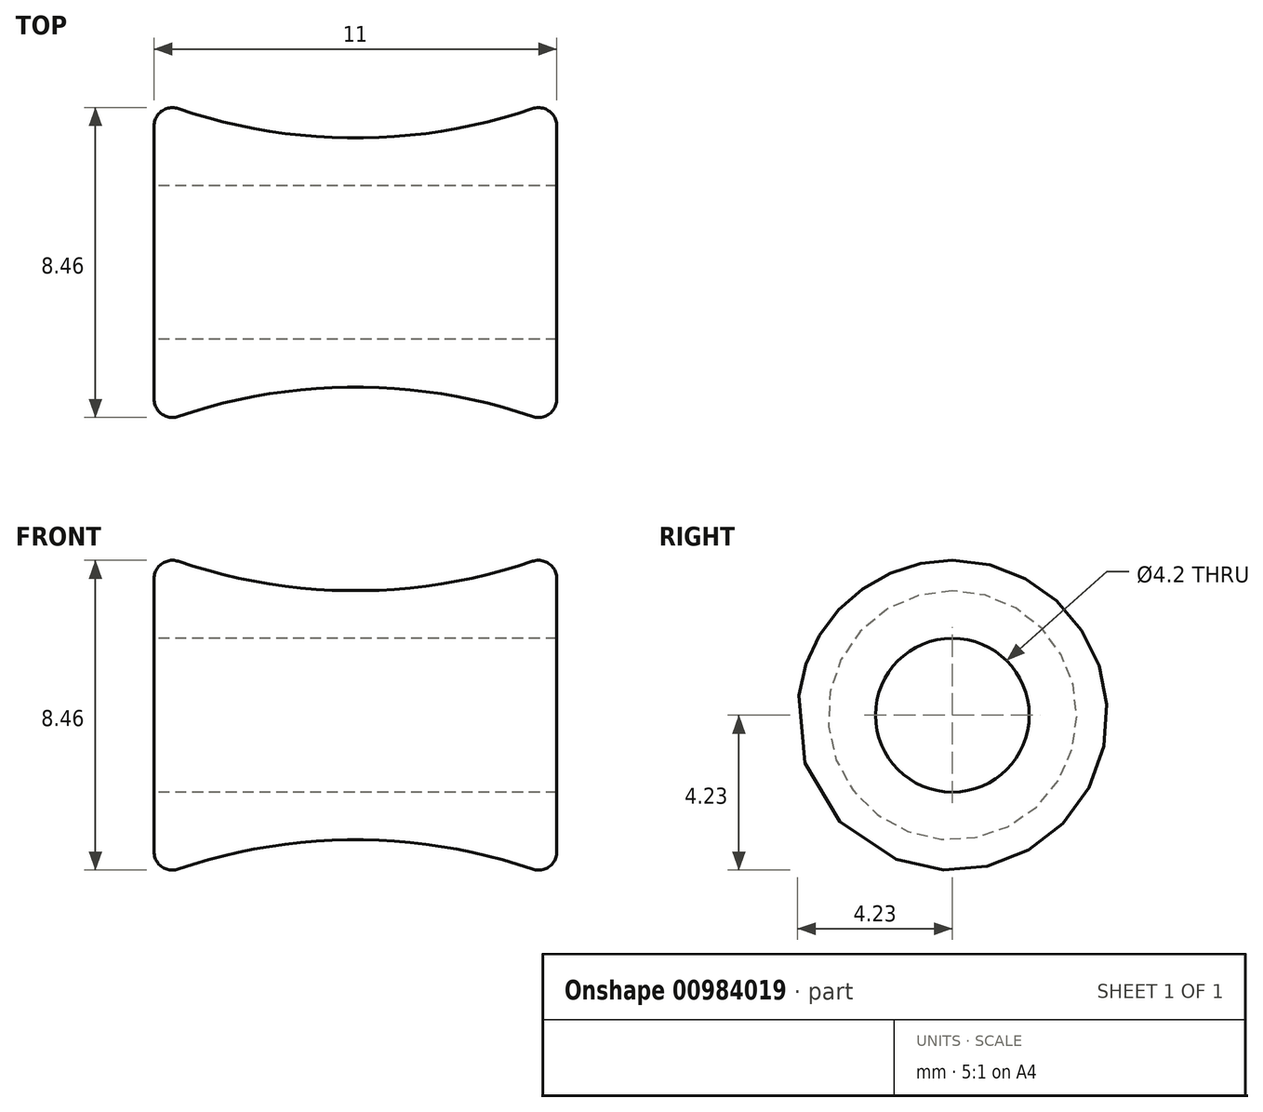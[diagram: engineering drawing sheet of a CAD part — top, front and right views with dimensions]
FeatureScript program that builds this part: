
annotation { "Feature Type Name" : "Feature", "Feature Type Description" : "" }
export const myFeature = defineFeature(function(context is Context, id is Id, definition is map)
    precondition{}
    {
        {
            var Q0;
            Q0=qCreatedBy(makeId("Top.planeOp"),FACE);
            var sketch = newSketch(context, id + "F0", { "sketchPlane" : qUnion([Q0])});
            skLineSegment(sketch, "E0", {"start": v(-11.64, 0) * mm, "end": v(10.67, 0) * mm, "construction": true});
            skLineSegment(sketch, "E1", {"start": v(-5.37, 2.1) * mm, "end": v(5.63, 2.1) * mm});
            skLineSegment(sketch, "E2", {"start": v(5.63, 2.1) * mm, "end": v(5.63, 4.44) * mm});
            skLineSegment(sketch, "E3", {"start": v(-5.37, 2.1) * mm, "end": v(-5.37, 4.44) * mm});
            skArc(sketch, "E4", {"start": v(-5.37, 4.44) * mm, "mid": v(0.13, 3.4) * mm, "end": v(5.63, 4.44) * mm});
            skSolve(sketch);
        }
        {
            var Q0;
            Q0=makeQuery(id+"F0.imprint","IMPRINT",FACE,{"disambiguationData":[TD([[makeQuery(id+"F0.imprint","IMPRINT",EDGE,{"derivedFrom":sQuery(id+"F0.wireOp",EDGE,"E1")}),1.0]])]});
            var Q1;
            Q1=sQuery(id+"F0.wireOp",EDGE,"E0");
            revolve(context, id + "F1", {"surfaceOperationType" : NewSurfaceOperationType.NEW, "entities" : qUnion([Q0]), "axis" : qUnion([Q1]), "revolveType" : RevolveType.FULL});
        }
        {
            var Q0;
            Q0=makeQuery(id+"F1.opRevolve","SWEPT_EDGE",EDGE,{"disambiguationData":[OSD([sQuery(id+"F0.wireOp",EDGE,"E2"),sQuery(id+"F0.wireOp",EDGE,"E4")])]});
            var Q1;
            Q1=makeQuery(id+"F1.opRevolve","SWEPT_EDGE",EDGE,{"disambiguationData":[OSD([sQuery(id+"F0.wireOp",EDGE,"E3"),sQuery(id+"F0.wireOp",EDGE,"E4")])]});
            fillet(context, id + "F2", {"entities" : qUnion([Q0, Q1]), "radius" : 0.5 * mm, "tangentPropagation" : true, "allowEdgeOverflow" : false});
        }
    });
